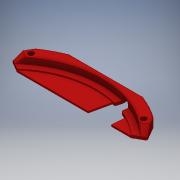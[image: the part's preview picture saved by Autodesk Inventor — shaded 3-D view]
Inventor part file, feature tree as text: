
AUTODESK INVENTOR PART (.ipt)
format: ipt  version: 2018 (Build 220112000, 112)  size: 409,600 bytes
history: native  units: mm
features: fillet x16, extrude x9, sketch x9, chamfer x2, hole x1
ambient origin geometry x8: Origin, YZ Plane, XZ Plane, XY Plane, X Axis, Y Axis, Z Axis, Center Point
bodies: Solid1 (feature_tree)
feature tree (37):
  extrude  "Extrusion1"  Depth=334.0mm
  extrude  "Extrusion2"  TaperAngle=150.0deg  [1 undecoded]
  extrude  "Extrusion3"  TaperAngle=30.0deg  [1 undecoded]
  hole  "Hole1"  [1 undecoded]
  chamfer  "Chamfer1"  Distance=3.0mm
  chamfer  "Chamfer2"  Distance=21.5mm
  fillet  "Fillet1"  [1 undecoded]
  fillet  "Fillet2"  Radius=30.0mm
  fillet  "Fillet3"  [1 undecoded]
  fillet  "Fillet4"  Radius=2.0mm
  fillet  "Fillet5"  Radius=208.768749mm
  fillet  "Fillet6"  Radius=134.029613mm
  fillet  "Fillet7"  Radius=30.0mm
  fillet  "Fillet8"  Radius=30.0mm
  fillet  "Fillet9"  Radius=13.0mm
  fillet  "Fillet10"  Radius=156.0mm
  fillet  "Fillet11"  Radius=23.038346mm
  extrude  "Extrusion5"  Depth=2.0mm
  extrude  "Extrusion6"  TaperAngle=150.0deg  [1 undecoded]
  extrude  "Extrusion7"  Depth=2.0mm
  extrude  "Extrusion8"  Depth=2.0mm
  extrude  "Extrusion9"  Depth=2.0mm
  extrude  "Extrusion10"  Depth=2.0mm
  fillet  "Fillet13"  Radius=11.0mm
  fillet  "Fillet14"  Radius=10.75mm
  fillet  "Fillet15"  Radius=10.0mm
  fillet  "Fillet17"  Radius=10.75mm
  fillet  "Fillet18"  Radius=10.0mm
  sketch  "Sketch2"  dims[d0=312.0mm d1=334.0mm]
  sketch  "Sketch3"  dims[d3=21.5mm d4=150.0deg]
  sketch  "Sketch5"  dims[d5=21.5mm d6=30.0deg]
  sketch  "Sketch9"  dims[d8=30.0mm d9=60.0deg]
  sketch  "Sketch10"  dims[d10=30.0mm]
  sketch  "Sketch12"  dims[d11=120.0deg d13=3.0mm d14=0.0mm]
  sketch  "Sketch14"  dims[d18=21.5mm]
  sketch  "Sketch15"  dims[d19=150.0deg]
  sketch  "Sketch16"  dims[d20=30.0mm d21=21.5mm d22=30.0deg d23=30.0mm d24=120.0deg d26=2.0mm d27=0.0mm d32=208.768749mm d33=134.029613mm d36=30.0mm d40=30.0mm d43=13.0mm d44=0.0mm d46=156.0mm d47=23.038346mm d48=21.5mm d49=150.0deg d50=11.0mm d51=156.0mm d52=21.5mm d53=28.274334mm d54=11.0mm d55=10.75mm d56=10.0mm d57=10.75mm d58=10.0mm d59=10.0mm d60=10.0mm d61=5.0mm d62=6.0mm d63=10.0mm d64=13.0mm d65=90.0deg d66=18.0mm d67=0.0mm d68=13.0mm d69=2.0mm d70=45.0deg d71=13.0mm d72=2.0mm d73=45.0deg d74=2.0mm d75=2.0mm d76=2.0mm d77=2.0mm d78=2.0mm d79=2.0mm d80=2.0mm d81=2.0mm d82=2.0mm d83=2.0mm d84=2.0mm d104=18.0mm d105=0.0mm d106=16.0mm d107=5.0mm d108=40.7mm d109=0.0mm d110=334.0mm d111=312.0mm d112=14.430382mm d113=5.0mm d114=0.0mm d119=300.0mm d120=312.0mm d121=13.381439mm d122=10.166543mm d123=30.1mm d126=16.500343mm d127=3.0mm d128=0.0mm d129=312.0mm d130=13.189453mm d132=13.538519mm d133=3.0mm d134=0.0mm d135=34.383516mm d136=36.390274mm d137=119.730191mm d138=3.0mm d139=16.086mm d140=0.05mm d141=0.0mm d143=3.0mm d144=3.0mm d145=3.0mm d150=2.0mm d151=2.0mm]
note: 6 required parameter values undecoded (feature->parameter linkage not recoverable at this tier; creation-order binding heuristic only, values carry confidence <= 0.55)
